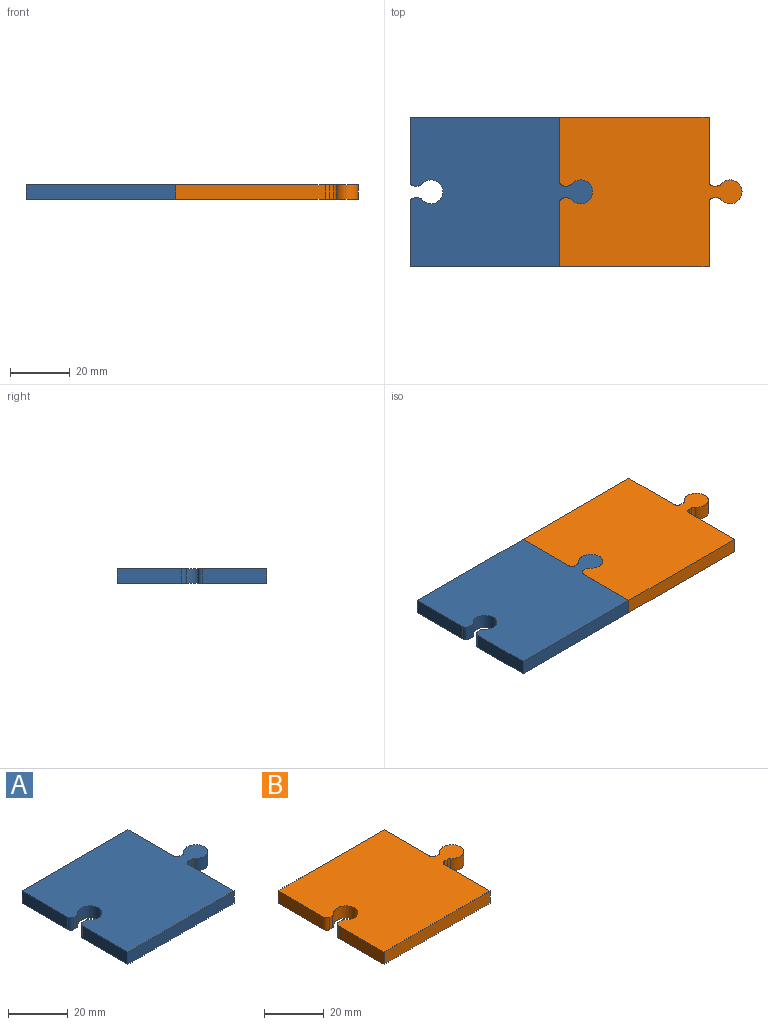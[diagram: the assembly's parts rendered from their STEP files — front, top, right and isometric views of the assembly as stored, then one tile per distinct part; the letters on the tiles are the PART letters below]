
ASSEMBLY  parts=2 mates=1
PART A: 22 faces, bbox 61x50x5 mm
  f0: plane 5x1.24mm, normal (0,-1,0), area 6.2mm2, adj f1,f19,f20,f21
  f1: cylinder r=1.5mm len=5mm, axis (0,0,-1), area 6.7mm2, adj f0,f2,f20,f21
  f2: cylinder r=4mm len=8mm, axis (0,0,-1), area 98.1mm2, adj f1,f3,f20,f21
  f3: cylinder r=1.5mm len=5mm, axis (0,0,-1), area 6.5mm2, adj f2,f4,f20,f21
  f4: plane 5x1.34mm, normal (0,1,0), area 6.7mm2, adj f3,f5,f20,f21
  f5: cylinder r=1.5mm len=5mm, axis (0,0,-1), area 11.8mm2, adj f4,f6,f20,f21
  f6: plane 21.5x5mm, normal (-1,0,0), area 107.5mm2, adj f5,f7,f20,f21
  f7: plane 50x5mm, normal (0,-1,0), area 250mm2, adj f6,f8,f20,f21
  f8: plane 21.5x5mm, normal (1,0,0), area 107.5mm2, adj f7,f9,f20,f21
  f9: cylinder r=1.5mm len=5mm, axis (0,0,-1), area 11.8mm2, adj f8,f10,f20,f21
  f10: plane 5x1.33mm, normal (0,-1,0), area 6.7mm2, adj f9,f11,f20,f21
  f11: cylinder r=1.5mm len=5mm, axis (0,0,-1), area 6.5mm2, adj f10,f12,f20,f21
  f12: cylinder r=4mm len=8mm, axis (0,0,-1), area 98.1mm2, adj f11,f13,f20,f21
  f13: cylinder r=1.5mm len=5mm, axis (0,0,-1), area 6.7mm2, adj f12,f14,f20,f21
  f14: plane 5x1.24mm, normal (0,1,0), area 6.2mm2, adj f13,f15,f20,f21
  f15: cylinder r=1.5mm len=5mm, axis (0,0,-1), area 11.8mm2, adj f14,f16,f20,f21
  f16: plane 21.5x5mm, normal (1,0,0), area 107.5mm2, adj f15,f17,f20,f21
  f17: plane 50x5mm, normal (0,1,0), area 250mm2, adj f16,f18,f20,f21
  f18: plane 21.5x5mm, normal (-1,0,0), area 107.5mm2, adj f17,f19,f20,f21
  f19: cylinder r=1.5mm len=5mm, axis (0,0,-1), area 11.8mm2, adj f0,f18,f20,f21
  f20: plane 61.03x50mm, normal (0,0,1), area 2500mm2, adj f0,f1,f2,f3,f4,f5,f6,f7
  f21: plane 61.03x50mm, normal (0,0,-1), area 2500mm2, adj f0,f1,f2,f3,f4,f5,f6,f7
PART B: 22 faces, bbox 61x50x5 mm
  f0: plane 5x1.24mm, normal (0,-1,0), area 6.2mm2, adj f1,f19,f20,f21
  f1: cylinder r=1.5mm len=5mm, axis (0,0,-1), area 6.7mm2, adj f0,f2,f20,f21
  f2: cylinder r=4mm len=8mm, axis (0,0,-1), area 98.1mm2, adj f1,f3,f20,f21
  f3: cylinder r=1.5mm len=5mm, axis (0,0,-1), area 6.5mm2, adj f2,f4,f20,f21
  f4: plane 5x1.34mm, normal (0,1,0), area 6.7mm2, adj f3,f5,f20,f21
  f5: cylinder r=1.5mm len=5mm, axis (0,0,-1), area 11.8mm2, adj f4,f6,f20,f21
  f6: plane 21.5x5mm, normal (-1,0,0), area 107.5mm2, adj f5,f7,f20,f21
  f7: plane 50x5mm, normal (0,-1,0), area 250mm2, adj f6,f8,f20,f21
  f8: plane 21.5x5mm, normal (1,0,0), area 107.5mm2, adj f7,f9,f20,f21
  f9: cylinder r=1.5mm len=5mm, axis (0,0,-1), area 11.8mm2, adj f8,f10,f20,f21
  f10: plane 5x1.33mm, normal (0,-1,0), area 6.7mm2, adj f9,f11,f20,f21
  f11: cylinder r=1.5mm len=5mm, axis (0,0,-1), area 6.5mm2, adj f10,f12,f20,f21
  f12: cylinder r=4mm len=8mm, axis (0,0,-1), area 98.1mm2, adj f11,f13,f20,f21
  f13: cylinder r=1.5mm len=5mm, axis (0,0,-1), area 6.7mm2, adj f12,f14,f20,f21
  f14: plane 5x1.24mm, normal (0,1,0), area 6.2mm2, adj f13,f15,f20,f21
  f15: cylinder r=1.5mm len=5mm, axis (0,0,-1), area 11.8mm2, adj f14,f16,f20,f21
  f16: plane 21.5x5mm, normal (1,0,0), area 107.5mm2, adj f15,f17,f20,f21
  f17: plane 50x5mm, normal (0,1,0), area 250mm2, adj f16,f18,f20,f21
  f18: plane 21.5x5mm, normal (-1,0,0), area 107.5mm2, adj f17,f19,f20,f21
  f19: cylinder r=1.5mm len=5mm, axis (0,0,-1), area 11.8mm2, adj f0,f18,f20,f21
  f20: plane 61.03x50mm, normal (0,0,1), area 2500mm2, adj f0,f1,f2,f3,f4,f5,f6,f7
  f21: plane 61.03x50mm, normal (0,0,-1), area 2500mm2, adj f0,f1,f2,f3,f4,f5,f6,f7
PLACE A t=(-13.01,0.29,8.17)mm
PLACE B t=(14.18,24.9,8.17)mm
MATE fastened A.f12 <-> B.f2  axis (0,0,1) through (-5.99,25.34,13.17)mm
